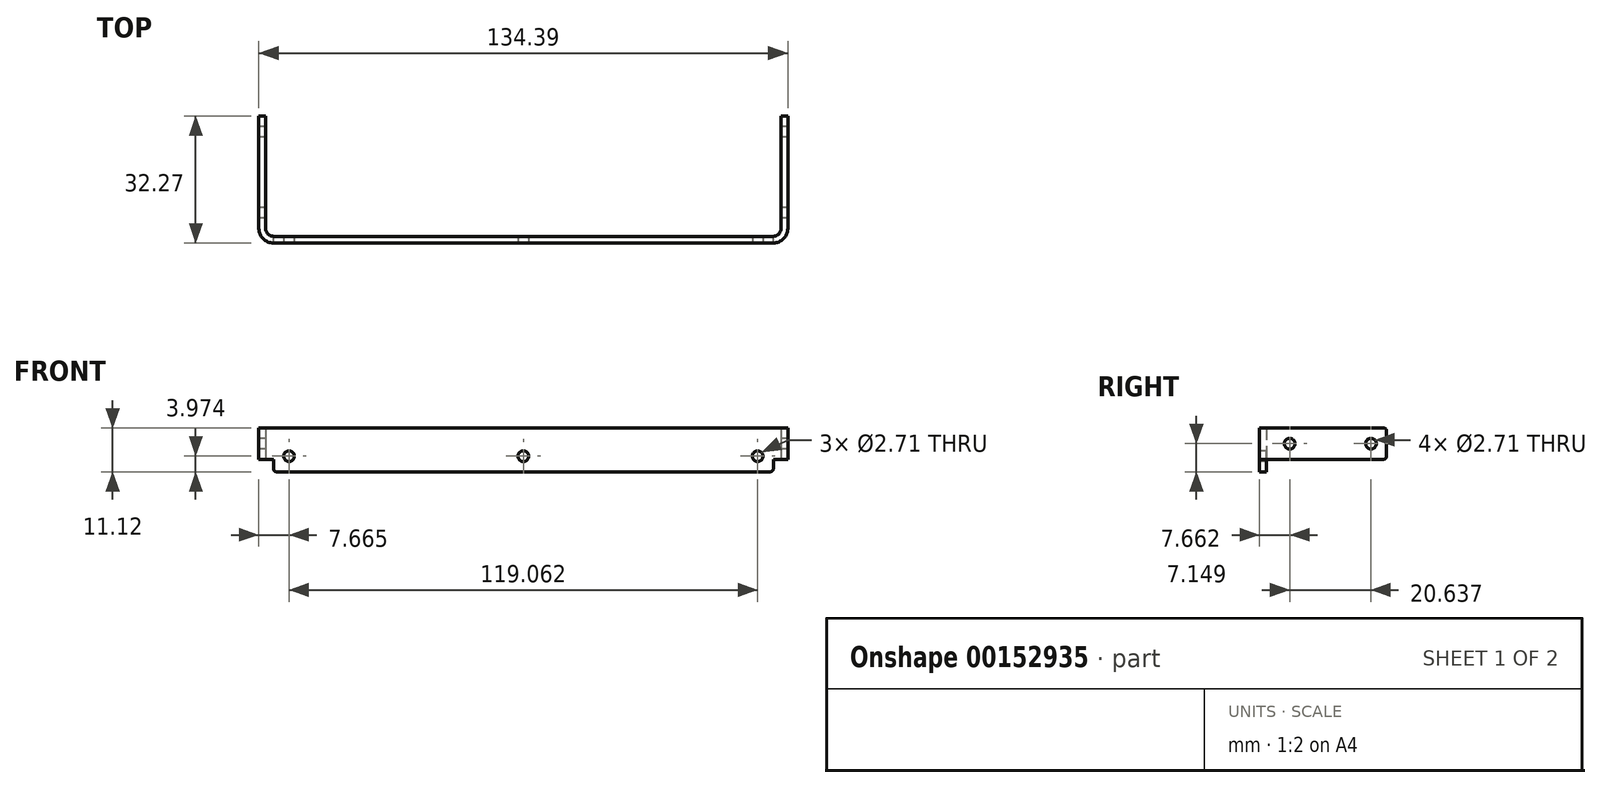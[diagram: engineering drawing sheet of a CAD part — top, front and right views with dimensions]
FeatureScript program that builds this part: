
annotation { "Feature Type Name" : "Feature", "Feature Type Description" : "" }
export const myFeature = defineFeature(function(context is Context, id is Id, definition is map)
    precondition{}
    {
        {
            var Q0;
            Q0=qCreatedBy(makeId("Top.planeOp"),FACE);
            var sketch = newSketch(context, id + "F0", { "sketchPlane" : qUnion([Q0])});
            skLineSegment(sketch, "E0.bottom", {"start": v(0, 0) * mm, "end": v(-130.97, 0) * mm});
            skLineSegment(sketch, "E0.top", {"start": v(1.7, -1.7) * mm, "end": v(-132.68, -1.7) * mm});
            skLineSegment(sketch, "E1.top", {"start": v(-130.97, 30.56) * mm, "end": v(-132.68, 30.56) * mm});
            skLineSegment(sketch, "E1.left", {"start": v(-130.97, 0) * mm, "end": v(-130.97, 30.56) * mm});
            skLineSegment(sketch, "E1.right", {"start": v(-132.68, -1.7) * mm, "end": v(-132.68, 30.56) * mm});
            skLineSegment(sketch, "E2.top", {"start": v(0, 30.56) * mm, "end": v(1.7, 30.56) * mm});
            skLineSegment(sketch, "E2.left", {"start": v(0, 0) * mm, "end": v(0, 30.56) * mm});
            skLineSegment(sketch, "E2.right", {"start": v(1.7, -1.7) * mm, "end": v(1.7, 30.56) * mm});
            skLineSegment(sketch, "E3", {"start": v(-65.48, 0) * mm, "end": v(-65.48, -1.7) * mm, "construction": true});
            skSolve(sketch);
        }
        {
            var Q0;
            Q0=qSketchRegion(id+"F0",true);
            extrude(context, id + "F1", {"entities" : qUnion([Q0]), "depth" : 7.94 * mm});
        }
        {
            var Q0;
            Q0=makeQuery(id+"FcdIcV9w6YY9zah_1.opExtrude","CAP_EDGE",EDGE,{"disambiguationData":[OSD([sQuery(id+"FU7sgaIbCbRhSfr_1.wireOp",EDGE,"F29Sxc5V-O2cl-wjtz-gx5o-reTTBG7m1pNU.top")])],"isStart":true});
            var Q1;
            Q1=makeQuery(id+"FcdIcV9w6YY9zah_1.opExtrude","CAP_EDGE",EDGE,{"disambiguationData":[OSD([sQuery(id+"FU7sgaIbCbRhSfr_1.wireOp",EDGE,"yv2bQU74-Eht6-uYuo-WBF2-3C4kyuaz0slr.top")])],"isStart":true});
            var Q2;
            Q2=makeQuery(id+"F1.opExtrude","SWEPT_EDGE",EDGE,{"disambiguationData":[OSD([sQuery(id+"F0.wireOp",EDGE,"E0.bottom"),sQuery(id+"F0.wireOp",EDGE,"E2.left")])]});
            var Q3;
            Q3=makeQuery(id+"F1.opExtrude","SWEPT_EDGE",EDGE,{"disambiguationData":[OSD([sQuery(id+"F0.wireOp",EDGE,"E0.bottom"),sQuery(id+"F0.wireOp",EDGE,"E1.left")])]});
            fillet(context, id + "F2", {"entities" : qUnion([Q0, Q1, Q2, Q3]), "radius" : 1.98 * mm, "tangentPropagation" : true, "allowEdgeOverflow" : false});
        }
        {
            var Q0;
            Q0=makeQuery(id+"FkwQQH4eT4IjhdK_1.opExtrude","CAP_EDGE",EDGE,{"disambiguationData":[OSD([sQuery(id+"FvDFSbhwMPyTNrQ_1.wireOp",EDGE,"223FG13h-YrEq-unoX-9EOi-DwKLLmwbrteD.top")])],"isStart":false});
            var Q1;
            Q1=makeQuery(id+"F1.opExtrude","SWEPT_EDGE",EDGE,{"disambiguationData":[OSD([sQuery(id+"F0.wireOp",EDGE,"E0.top"),sQuery(id+"F0.wireOp",EDGE,"E2.right")])]});
            var Q2;
            Q2=makeQuery(id+"F1.opExtrude","SWEPT_EDGE",EDGE,{"disambiguationData":[OSD([sQuery(id+"F0.wireOp",EDGE,"E0.top"),sQuery(id+"F0.wireOp",EDGE,"E1.right")])]});
            var Q3;
            Q3=makeQuery(id+"F2kHonbXZaQoFrR_1.opExtrude","CAP_EDGE",EDGE,{"disambiguationData":[OSD([sQuery(id+"FsAbJG8AZOSwdHE_1.wireOp",EDGE,"WRaIy3id-o2EU-qHqw-IwdC-eHQZRSiK4KpF.bottom")])],"isStart":false});
            fillet(context, id + "F3", {"entities" : qUnion([Q0, Q1, Q2, Q3]), "radius" : 3.7 * mm, "tangentPropagation" : true, "allowEdgeOverflow" : false});
        }
        {
            var Q0;
            Q0=makeQuery(id+"F1.opExtrude","SWEPT_FACE",FACE,{"disambiguationData":[OSD([sQuery(id+"F0.wireOp",EDGE,"E1.right")])]});
            var sketch = newSketch(context, id + "F4", { "sketchPlane" : qUnion([Q0])});
            skLineSegment(sketch, "E4", {"start": v(-30.56, 3.97) * mm, "end": v(-26.59, 3.97) * mm, "construction": true});
            skLineSegment(sketch, "E5", {"start": v(-26.59, 3.97) * mm, "end": v(-5.95, 3.97) * mm, "construction": true});
            skLineSegment(sketch, "E6", {"start": v(-5.95, 3.97) * mm, "end": v(-1.98, 3.97) * mm, "construction": true});
            skLineSegment(sketch, "E7", {"start": v(-26.59, 3.97) * mm, "end": v(-26.59, 0) * mm, "construction": true});
            skCircle(sketch, "E8", {"center": v(-26.59, 3.97) * mm, "radius": 1.35 * mm});
            skCircle(sketch, "E9", {"center": v(-5.95, 3.97) * mm, "radius": 1.35 * mm});
            skSolve(sketch);
        }
        {
            var Q0;
            Q0 = qSketchRegion(id + "F4", true);
            var Q1;
            Q1=makeQuery(id+"F1.opExtrude","SWEPT_FACE",FACE,{"disambiguationData":[OSD([sQuery(id+"F0.wireOp",EDGE,"E2.right")])]});
            extrude(context, id + "F5", {"entities" : qUnion([Q0]), "operationType" : NewBodyOperationType.REMOVE, "endBound" : BoundingType.UP_TO_SURFACE, "oppositeDirection" : true, "endBoundEntityFace" : qUnion([Q1]), "depth" : 25.4 * mm});
        }
        {
            var Q0;
            Q0=makeQuery(id+"F1.opExtrude","CAP_FACE",FACE,{"disambiguationData":[OSD([sQuery(id+"F0.wireOp",EDGE,"E0.bottom"),sQuery(id+"F0.wireOp",EDGE,"E0.top"),sQuery(id+"F0.wireOp",EDGE,"E1.top"),sQuery(id+"F0.wireOp",EDGE,"E1.left"),sQuery(id+"F0.wireOp",EDGE,"E1.right"),sQuery(id+"F0.wireOp",EDGE,"E2.top"),sQuery(id+"F0.wireOp",EDGE,"E2.left"),sQuery(id+"F0.wireOp",EDGE,"E2.right")])],"isStart":true});
            var sketch = newSketch(context, id + "F6", { "sketchPlane" : qUnion([Q0])});
            skLineSegment(sketch, "E10.bottom", {"start": v(-128.98, 1.7) * mm, "end": v(-1.98, 1.7) * mm});
            skLineSegment(sketch, "E10.top", {"start": v(-128.98, 0) * mm, "end": v(-1.98, 0) * mm});
            skLineSegment(sketch, "E10.left", {"start": v(-128.98, 1.7) * mm, "end": v(-128.98, 0) * mm});
            skLineSegment(sketch, "E10.right", {"start": v(-1.98, 1.7) * mm, "end": v(-1.98, 0) * mm});
            skSolve(sketch);
        }
        {
            var Q0;
            Q0 = qSketchRegion(id + "F6", true);
            extrude(context, id + "F7", {"entities" : qUnion([Q0]), "operationType" : NewBodyOperationType.ADD, "depth" : 3.17 * mm});
        }
        {
            var Q0;
            Q0=makeQuery(id+"F1.opExtrude","SWEPT_FACE",FACE,{"disambiguationData":[OSD([sQuery(id+"F0.wireOp",EDGE,"E0.top")])]});
            var sketch = newSketch(context, id + "F8", { "sketchPlane" : qUnion([Q0])});
            skLineSegment(sketch, "E11.bottom", {"start": v(-128.98, -3.18) * mm, "end": v(-125.01, -3.18) * mm, "construction": true});
            skLineSegment(sketch, "E11.top", {"start": v(-128.98, 0.8) * mm, "end": v(-125.01, 0.8) * mm, "construction": true});
            skLineSegment(sketch, "E11.left", {"start": v(-128.98, -3.18) * mm, "end": v(-128.98, 0.8) * mm, "construction": true});
            skLineSegment(sketch, "E11.right", {"start": v(-125.01, -3.18) * mm, "end": v(-125.01, 0.8) * mm, "construction": true});
            skLineSegment(sketch, "E12.bottom", {"start": v(-1.98, -3.17) * mm, "end": v(-5.95, -3.17) * mm, "construction": true});
            skLineSegment(sketch, "E12.top", {"start": v(-1.98, 0.8) * mm, "end": v(-5.95, 0.8) * mm, "construction": true});
            skLineSegment(sketch, "E12.left", {"start": v(-1.98, -3.18) * mm, "end": v(-1.98, 0.8) * mm, "construction": true});
            skLineSegment(sketch, "E12.right", {"start": v(-5.95, -3.17) * mm, "end": v(-5.95, 0.8) * mm, "construction": true});
            skLineSegment(sketch, "E13", {"start": v(-125.01, 0.8) * mm, "end": v(-5.95, 0.8) * mm, "construction": true});
            skCircle(sketch, "E14", {"center": v(-125.01, 0.8) * mm, "radius": 1.35 * mm});
            skCircle(sketch, "E15", {"center": v(-65.48, 0.8) * mm, "radius": 1.35 * mm});
            skPoint(sketch, "E15.perimeterSnap0", {"position": v(-65.48, 0.8) * mm});
            skCircle(sketch, "E16", {"center": v(-5.95, 0.8) * mm, "radius": 1.35 * mm});
            skSolve(sketch);
        }
        {
            var Q0;
            Q0 = qSketchRegion(id + "F8", true);
            var Q1;
            Q1=makeQuery(id+"F1.opExtrude","SWEPT_FACE",FACE,{"disambiguationData":[OSD([sQuery(id+"F0.wireOp",EDGE,"E0.bottom")])]});
            extrude(context, id + "F9", {"entities" : qUnion([Q0]), "operationType" : NewBodyOperationType.REMOVE, "endBound" : BoundingType.UP_TO_SURFACE, "oppositeDirection" : true, "endBoundEntityFace" : qUnion([Q1]), "depth" : 25.4 * mm});
        }
        {
            var Q0;
            Q0=makeQuery(id+"F1.opExtrude","CAP_EDGE",EDGE,{"disambiguationData":[OSD([sQuery(id+"F0.wireOp",EDGE,"E2.top")])],"isStart":true});
            var Q1;
            Q1=makeQuery(id+"F1.opExtrude","CAP_EDGE",EDGE,{"disambiguationData":[OSD([sQuery(id+"F0.wireOp",EDGE,"E2.top")])],"isStart":false});
            var Q2;
            Q2=makeQuery(id+"F1.opExtrude","CAP_EDGE",EDGE,{"disambiguationData":[OSD([sQuery(id+"F0.wireOp",EDGE,"E1.top")])],"isStart":true});
            var Q3;
            Q3=makeQuery(id+"F1.opExtrude","CAP_EDGE",EDGE,{"disambiguationData":[OSD([sQuery(id+"F0.wireOp",EDGE,"E1.top")])],"isStart":false});
            var Q4;
            Q4=makeQuery(id+"F7.opExtrude","CAP_EDGE",EDGE,{"disambiguationData":[OSD([sQuery(id+"F6.wireOp",EDGE,"E10.left")])],"isStart":false});
            var Q5;
            Q5=makeQuery(id+"F7.opExtrude","CAP_EDGE",EDGE,{"disambiguationData":[OSD([sQuery(id+"F6.wireOp",EDGE,"E10.right")])],"isStart":false});
            fillet(context, id + "F10", {"entities" : qUnion([Q0, Q1, Q2, Q3, Q4, Q5]), "radius" : 0.76 * mm, "tangentPropagation" : true, "allowEdgeOverflow" : false});
        }
    });
